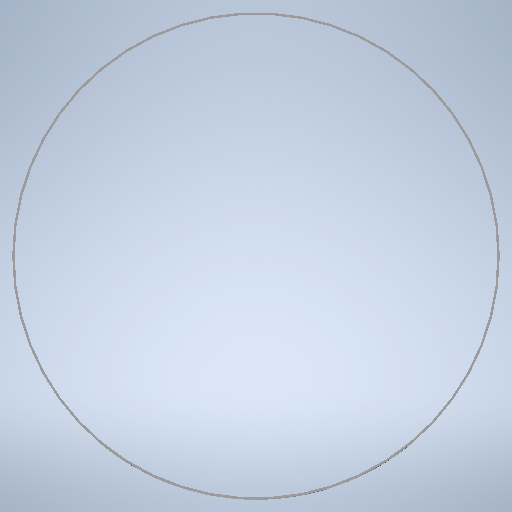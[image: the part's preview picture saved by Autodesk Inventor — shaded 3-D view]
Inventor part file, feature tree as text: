
AUTODESK INVENTOR PART (.ipt)
format: ipt  version: 2025.1 (Build 291241020, 241B)  size: 1,298,432 bytes
history: native  units: mm
features: other x9, sketch x6, extrude x4, revolve x1, plane x1
ambient origin geometry x8: Origin, YZ Plane, XZ Plane, XY Plane, X Axis, Y Axis, Z Axis, Center Point
bodies: Solid1 (feature_tree)
feature tree (21):
  revolve  "Revolution1"  [1 undecoded]
  extrude  "Extrusion1"  Depth=62.8144mm
  other  "floor angle sketch"
  other  "Feeder Plane"
  other  "Feeder horisont hight angle"
  other  "Feeder Work Plane"
  extrude  "Feeder Extrusion"  TaperAngle=0.0deg  [1 undecoded]
  other  "Inner Plane"
  other  "Inner horisont hight angle"
  other  "Inner Work Plane"
  extrude  "Inner Extrusion"  Depth=400.0mm
  other  "Outer Plane"
  sketch  "Sketch11"  dims[d16=400.0mm d17=180.0mm]
  plane  "Work Plane9"
  extrude  "Extrusion6"  Depth=400.0mm
  sketch  "Sketch1"  dims[d0=6.0mm d1=1770.0mm]
  sketch  "Sketch2"  dims[d2=1200.0mm d3=62.8144mm]
  sketch  "Sketch8"  dims[d4=530.0mm d10=0.0mm d11=0.0mm]
  sketch  "Sketch10"  dims[d12=400.0mm d15=200.0mm]
  sketch  "Sketch12"  dims[d34=1500.0mm d35=30.0deg d36=172.0mm d38=10.0mm d39=0.0mm d40=0.0mm d41=1300.0mm d42=91.0mm d43=0.0mm d44=0.0mm d45=0.0mm d46=700.0mm d47=92.0mm d48=10.0mm d49=0.0mm]
  other  "Definition1"
note: 2 required parameter values undecoded (feature->parameter linkage not recoverable at this tier; creation-order binding heuristic only, values carry confidence <= 0.55)